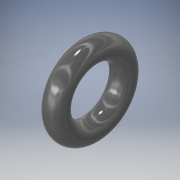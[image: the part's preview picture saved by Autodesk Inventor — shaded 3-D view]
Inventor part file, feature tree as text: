
AUTODESK INVENTOR PART (.ipt)
format: ipt  version: 2018 (Build 220112000, 112)  size: 153,088 bytes
history: native  units: in
note: dims shown in document units (in); Inventor stores cm internally (conversion verified against a paired STEP export)
features: revolve x1, sketch x1
ambient origin geometry x8: Origin, YZ Plane, XZ Plane, XY Plane, X Axis, Y Axis, Z Axis, Center Point
bodies: Solid1 (feature_tree)
feature tree (2):
  revolve  "Revolution1"  [1 undecoded]
  sketch  "Sketch1"  dims[d1=0.139in d2=0.1562in d3=90.0deg]
note: 1 required parameter value undecoded (feature->parameter linkage not recoverable at this tier; creation-order binding heuristic only, values carry confidence <= 0.55)
